# Revit family: E_FF130 Luminaire Cover
name_source: partatom
category: Specialty Equipment
revit_build: Autodesk Revit 2015 (Build: 20160512_0715(x64)
units: mm (PartAtom-declared; Revit-internal decimal feet)

## types (2) — shared parameters
Cutouts_Length = 600 mm
Height = 150 mm  [stored 0.492126 ft]
Manufacturer = Tenmat ltd
Material/Grade = Firefly 130
URL = https://www.tenmat.com
Youtube Clip = https://www.youtube.com

## per-type parameters (varying)
| type | Cutouts_Width | Description | Length_Bottom | Length_Top | Tenmat Item Number | Width_Bottom | Width_Top |
| 600x600mm | 600 mm | FF130 600x600mm Luminaire Cover | 719 mm  [stored 2.35892 ft] | 610 mm  [stored 2.00131 ft] | I130BM01550670073002 | 779 mm  [stored 2.55577 ft] | 670 mm  [stored 2.19816 ft] |
| 1200x600mm | 1200 mm | FF130 1200x600mm Luminaire Cover | 746 mm  [stored 2.44751 ft] | 650 mm  [stored 2.13255 ft] | I130BM01400750138002 | 1386 mm  [stored 4.54724 ft] | 1260 mm  [stored 4.13386 ft] |

note: [stored X ft] marks values corroborated as IEEE doubles in the binary element streams (Revit-internal decimal feet)

## geometry (parser evidence)
native form markers: Blend x2, Sweep x3
no freeform markers — native parametric forms only
